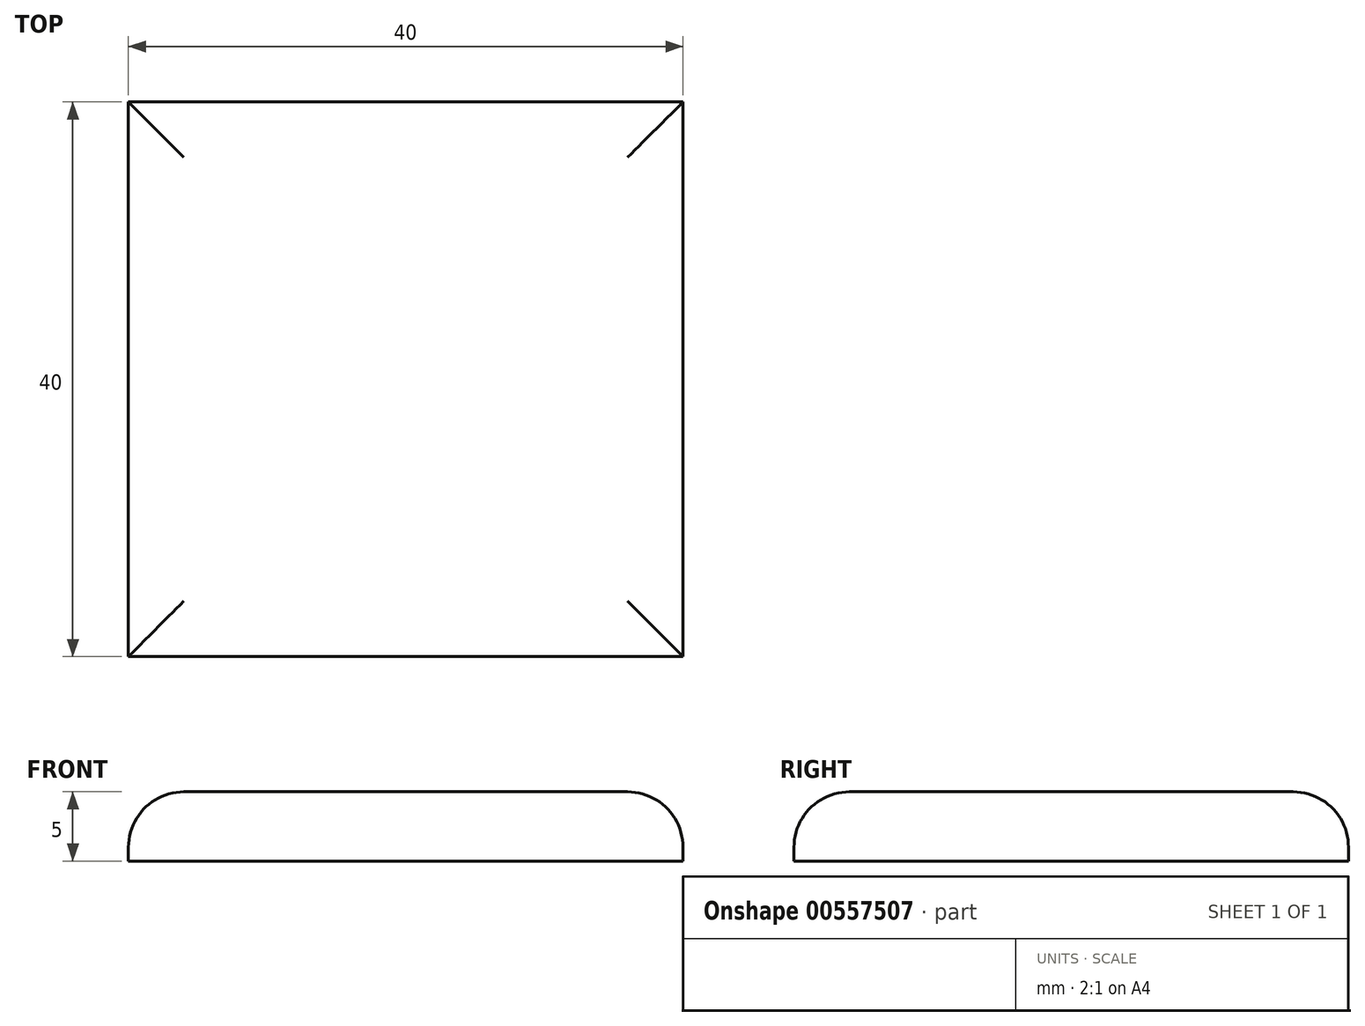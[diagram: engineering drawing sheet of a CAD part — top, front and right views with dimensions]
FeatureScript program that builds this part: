
annotation { "Feature Type Name" : "Feature", "Feature Type Description" : "" }
export const myFeature = defineFeature(function(context is Context, id is Id, definition is map)
    precondition{}
    {
        {
            var Q0;
            Q0=qCreatedBy(makeId("Top.planeOp"),FACE);
            var sketch = newSketch(context, id + "F0", { "sketchPlane" : qUnion([Q0])});
            skLineSegment(sketch, "E0.bottom", {"start": v(0, 0) * mm, "end": v(40, 0) * mm});
            skLineSegment(sketch, "E0.top", {"start": v(0, 40) * mm, "end": v(40, 40) * mm});
            skLineSegment(sketch, "E0.left", {"start": v(0, 0) * mm, "end": v(0, 40) * mm});
            skLineSegment(sketch, "E0.right", {"start": v(40, 0) * mm, "end": v(40, 40) * mm});
            skSolve(sketch);
        }
        {
            var Q0;
            Q0=makeQuery(id+"F0.imprint","IMPRINT",FACE,{"disambiguationData":[TD([[makeQuery(id+"F0.imprint","IMPRINT",EDGE,{"derivedFrom":sQuery(id+"F0.wireOp",EDGE,"E0.bottom")}),1.0]])]});
            extrude(context, id + "F1", {"entities" : qUnion([Q0]), "depth" : 5 * mm, "offsetDistance" : 25 * mm});
        }
        {
            var Q0;
            Q0=makeQuery(id+"F1.opExtrude","CAP_FACE",FACE,{"disambiguationData":[OSD([sQuery(id+"F0.wireOp",EDGE,"E0.bottom"),sQuery(id+"F0.wireOp",EDGE,"E0.top"),sQuery(id+"F0.wireOp",EDGE,"E0.left"),sQuery(id+"F0.wireOp",EDGE,"E0.right")])],"isStart":false});
            fillet(context, id + "F2", {"entities" : qUnion([Q0]), "radius" : 4 * mm, "tangentPropagation" : true, "allowEdgeOverflow" : false});
        }
    });
